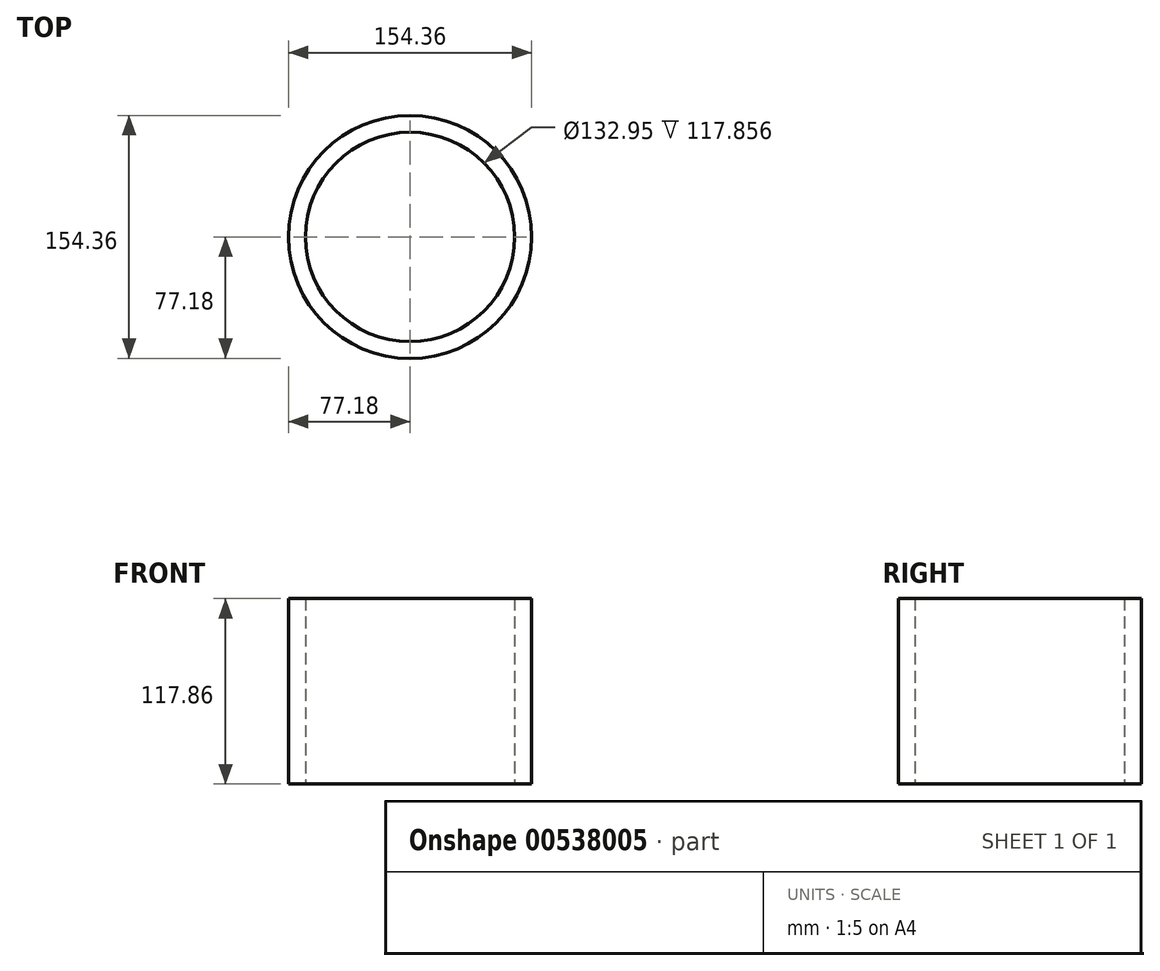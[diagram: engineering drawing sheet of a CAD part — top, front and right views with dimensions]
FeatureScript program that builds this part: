
annotation { "Feature Type Name" : "Feature", "Feature Type Description" : "" }
export const myFeature = defineFeature(function(context is Context, id is Id, definition is map)
    precondition{}
    {
        {
            var Q0;
            Q0=qCreatedBy(makeId("Top.planeOp"),FACE);
            var sketch = newSketch(context, id + "F0", { "sketchPlane" : qUnion([Q0])});
            skCircle(sketch, "E0", {"center": v(0, 0) * mm, "radius": 77.18 * mm});
            skCircle(sketch, "E1", {"center": v(0, 0) * mm, "radius": 66.48 * mm});
            skSolve(sketch);
        }
        {
            var Q0;
            Q0 = qSketchRegion(id + "F0", true);
            extrude(context, id + "F1", {"entities" : qUnion([Q0]), "depth" : 25.4 * mm, "offsetDistance" : 25.4 * mm});
        }
        {
            var Q0;
            Q0=makeQuery(id+"F1.opExtrude","CAP_FACE",FACE,{"disambiguationData":[OSD([sQuery(id+"F0.wireOp",EDGE,"E0"),sQuery(id+"F0.wireOp",EDGE,"E1")])],"isStart":true});
            var Q1;
            Q1=makeQuery(id+"F1.opExtrude","CAP_FACE",FACE,{"disambiguationData":[OSD([sQuery(id+"F0.wireOp",EDGE,"E0"),sQuery(id+"F0.wireOp",EDGE,"E1")])],"isStart":false});
            extrude(context, id + "F2", {"entities" : qUnion([Q0, Q1]), "operationType" : NewBodyOperationType.ADD, "depth" : 25.4 * mm, "offsetDistance" : 25.4 * mm});
        }
        {
            var Q0;
            Q0=makeQuery(id+"F1.opExtrude","CAP_FACE",FACE,{"disambiguationData":[OSD([sQuery(id+"F0.wireOp",EDGE,"E0"),sQuery(id+"F0.wireOp",EDGE,"E1")])],"isStart":false});
            extrude(context, id + "F3", {"entities" : qUnion([Q0]), "operationType" : NewBodyOperationType.ADD, "depth" : 67.06 * mm, "offsetDistance" : 25.4 * mm});
        }
    });
